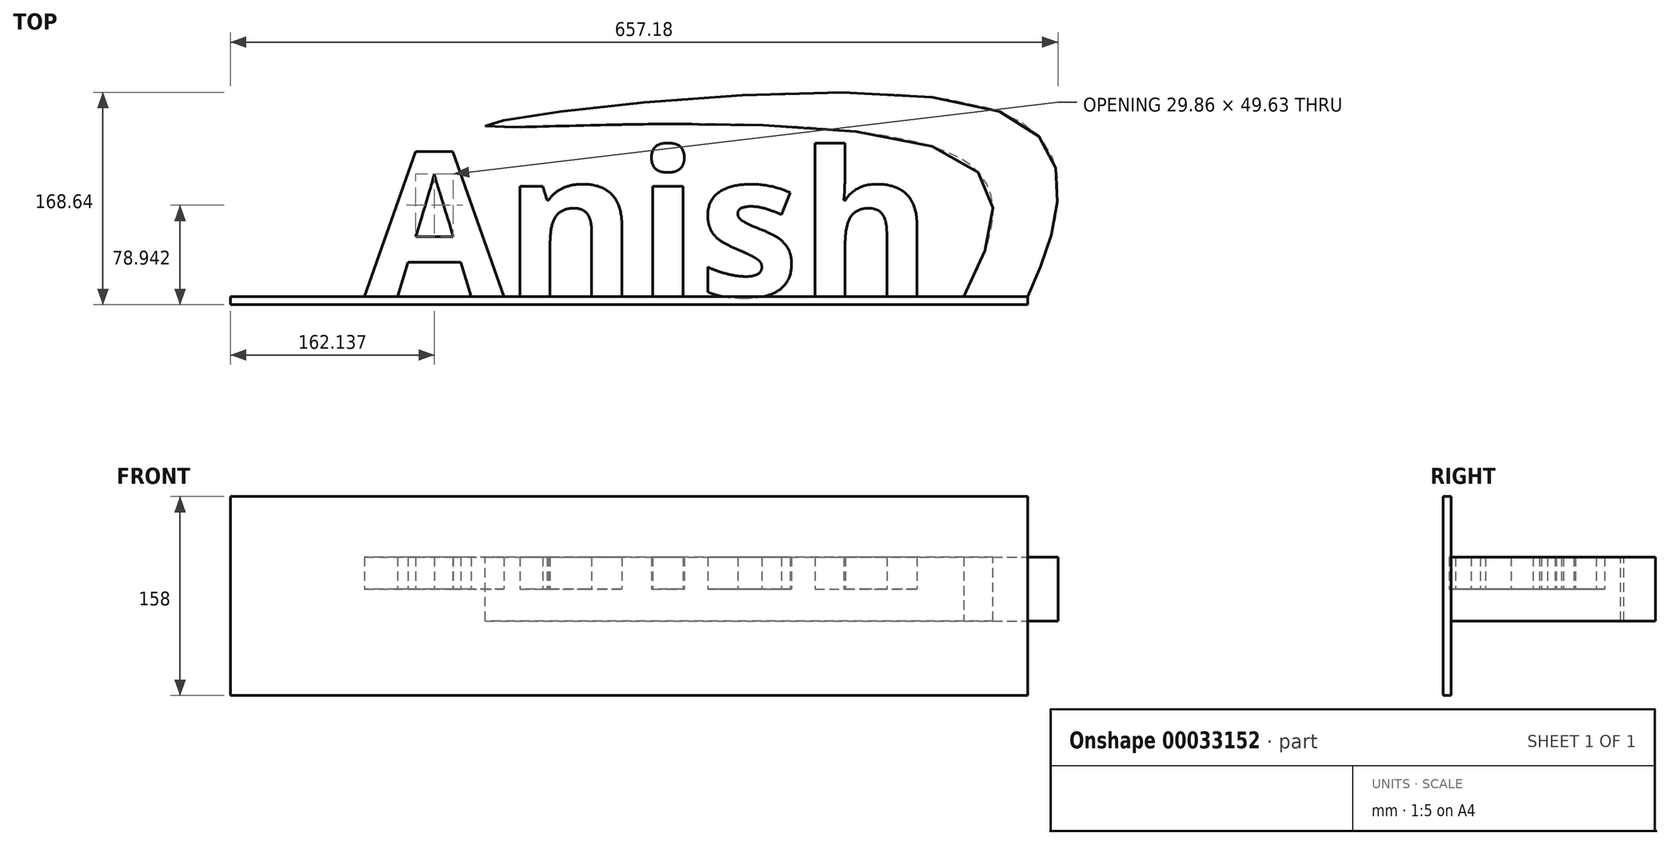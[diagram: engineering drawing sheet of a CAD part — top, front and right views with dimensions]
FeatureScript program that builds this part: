
annotation { "Feature Type Name" : "Feature", "Feature Type Description" : "" }
export const myFeature = defineFeature(function(context is Context, id is Id, definition is map)
    precondition{}
    {
        {
            var Q0;
            Q0=qCreatedBy(makeId("Top.planeOp"),FACE);
            var sketch = newSketch(context, id + "F0", { "sketchPlane" : qUnion([Q0])});
            skText(sketch, "E0", { "text": "Anish", "fontName": "OpenSans-Bold.ttf"});
            const initialGuessF0  = {"E0": [-0.20838, -0.0908, 1, 0, 0.11561]};
            skSetInitialGuess(sketch, initialGuessF0);
            skSolve(sketch);
        }
        {
            var Q0;
            Q0=makeQuery(id+"F0.imprint","IMPRINT",FACE,{"disambiguationData":[TD([[makeQuery(id+"F0.imprint","IMPRINT",EDGE,{"derivedFrom":sQuery(id+"F0.wireOp",EDGE,"E0.sketch_text.stroke-12")}),-1.0]])]});
            var Q1;
            Q1=makeQuery(id+"F0.imprint","IMPRINT",FACE,{"disambiguationData":[TD([[makeQuery(id+"F0.imprint","IMPRINT",EDGE,{"derivedFrom":sQuery(id+"F0.wireOp",EDGE,"E0.sketch_text.stroke-29")}),-1.0]])]});
            var Q2;
            Q2=makeQuery(id+"F0.imprint","IMPRINT",FACE,{"disambiguationData":[TD([[makeQuery(id+"F0.imprint","IMPRINT",EDGE,{"derivedFrom":sQuery(id+"F0.wireOp",EDGE,"E0.sketch_text.stroke-34")}),-1.0]])]});
            var Q3;
            Q3=makeQuery(id+"F0.imprint","IMPRINT",FACE,{"disambiguationData":[TD([[makeQuery(id+"F0.imprint","IMPRINT",EDGE,{"derivedFrom":sQuery(id+"F0.wireOp",EDGE,"E0.sketch_text.stroke-38")}),-1.0]])]});
            var Q4;
            Q4=makeQuery(id+"F0.imprint","IMPRINT",FACE,{"disambiguationData":[TD([[makeQuery(id+"F0.imprint","IMPRINT",EDGE,{"derivedFrom":sQuery(id+"F0.wireOp",EDGE,"E0.sketch_text.stroke-64")}),-1.0]])]});
            var Q5;
            Q5=makeQuery(id+"F0.imprint","IMPRINT",FACE,{"disambiguationData":[TD([[makeQuery(id+"F0.imprint","IMPRINT",EDGE,{"derivedFrom":sQuery(id+"F0.wireOp",EDGE,"E0.sketch_text.stroke-0")}),-1.0]])]});
            var Q6;
            Q6 = qSketchRegion(id + "F0", true);
            extrude(context, id + "F1", {"entities" : qUnion([Q0, Q1, Q2, Q3, Q4, Q5, Q6]), "depth" : 25.4 * mm});
        }
        {
            var Q0;
            Q0=makeQuery(id+"F1.opExtrude","SWEPT_FACE",FACE,{"disambiguationData":[OSD([sQuery(id+"F0.wireOp",EDGE,"E0.sketch_text.stroke-7")])]});
            var sketch = newSketch(context, id + "F2", { "sketchPlane" : qUnion([Q0])});
            skLineSegment(sketch, "E1.bottom", {"start": v(-314.97, 73.39) * mm, "end": v(318.34, 73.39) * mm});
            skLineSegment(sketch, "E1.top", {"start": v(-314.97, -84.6) * mm, "end": v(318.34, -84.6) * mm});
            skLineSegment(sketch, "E1.left", {"start": v(-314.97, 73.39) * mm, "end": v(-314.97, -84.6) * mm});
            skLineSegment(sketch, "E1.right", {"start": v(318.34, 73.39) * mm, "end": v(318.34, -84.6) * mm});
            skSolve(sketch);
        }
        {
            var Q0;
            Q0 = qSketchRegion(id + "F2", true);
            extrude(context, id + "F3", {"entities" : qUnion([Q0]), "depth" : 6.46 * mm});
        }
        {
            var Q0;
            Q0=qCreatedBy(makeId("Top.planeOp"),FACE);
            var sketch = newSketch(context, id + "F4", { "sketchPlane" : qUnion([Q0])});
            skLineSegment(sketch, "E2.0.0", {"start": v(-314.97, -90.8) * mm, "end": v(318.34, -90.8) * mm});
            skLineSegment(sketch, "E2.0.2", {"start": v(318.34, -90.8) * mm, "end": v(-314.97, -90.8) * mm});
            skFitSpline(sketch, "E3", {"points": [v(267.54, -90.8) * mm, v(262.47, 20.21) * mm, v(-112.44, 44.72) * mm, v(285.75, 59.63) * mm, v(341.64, -16.87) * mm, v(318.34, -90.8) * mm], "startDerivative": vector(452.64, 849.15) * mm, "endDerivative": vector(-233.84, -529.85) * mm});
            skSolve(sketch);
        }
        {
            var Q0;
            Q0 = qSketchRegion(id + "F4", true);
            extrude(context, id + "F5", {"entities" : qUnion([Q0]), "operationType" : NewBodyOperationType.ADD, "endBound" : BoundingType.SYMMETRIC, "depth" : 50.8 * mm});
        }
        {
            var Q0;
            Q0=qCreatedBy(makeId("Top.planeOp"),FACE);
            var sketch = newSketch(context, id + "F6", { "sketchPlane" : qUnion([Q0])});
            skFitSpline(sketch, "E4.0", {"points": [v(267.54, -90.8) * mm, v(290.79, -47.2) * mm, v(337.15, 77.2) * mm, v(-404.8, 12.7) * mm, v(323.66, 109.96) * mm, v(350.76, -16.31) * mm, v(328.37, -68.07) * mm, v(318.34, -90.8) * mm]});
            skPoint(sketch, "E5", {"position": v(216.29, 69.92) * mm});
            skPoint(sketch, "E6", {"position": v(-112.48, 44.94) * mm});
            skSolve(sketch);
        }
        {
            var Q0;
            Q0=makeQuery(id+"F3.opExtrude","CAP_FACE",FACE,{"disambiguationData":[OSD([sQuery(id+"F2.wireOp",EDGE,"E1.bottom"),sQuery(id+"F2.wireOp",EDGE,"E1.top"),sQuery(id+"F2.wireOp",EDGE,"E1.left"),sQuery(id+"F2.wireOp",EDGE,"E1.right")])],"isStart":true});
            var sketch = newSketch(context, id + "F7", { "sketchPlane" : qUnion([Q0])});
            skPoint(sketch, "E7", {"position": v(-156.04, -84.6) * mm});
            skPoint(sketch, "E8", {"position": v(137.95, -84.6) * mm});
            skPoint(sketch, "E9", {"position": v(314.97, -84.6) * mm});
            skSolve(sketch);
        }
    });
